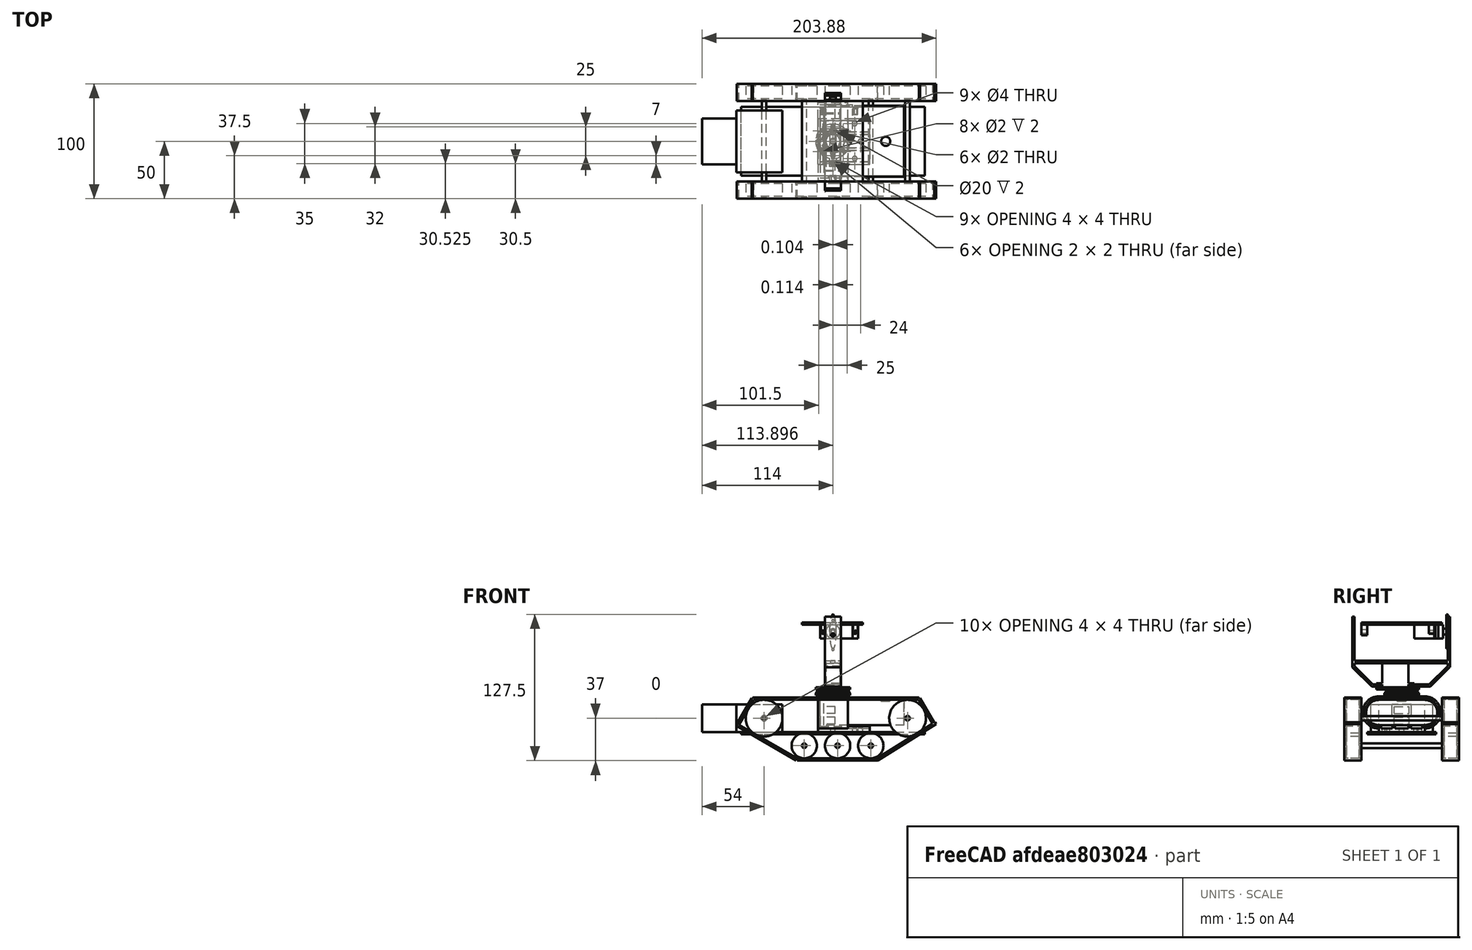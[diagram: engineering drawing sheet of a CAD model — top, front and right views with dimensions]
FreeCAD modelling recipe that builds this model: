
FCSTD DOCUMENT
Label: androidtank_8
License: CC-BY 3.0
LicenseURL: http://creativecommons.org/licenses/by/3.0/
objects: Part::Cylinder×56, Part::Box×36, Part::MultiFuse×25, Part::Sphere×8, Part::Cut×7, Part::FeaturePython×1, App::DocumentObjectGroup×1
note: 133 computed .brp shape members not serialized (recipe doc carries the construction recipe); baked Part::Feature solids carry a one-line shape summary decoded from their .brp

FEATURE [Part::Box] Box  label="MainFrame"
  Height = 2
  Length = 160
  Width = 60
FEATURE [Part::Box] Box001001  label="Moter Unit2"
  Height = 24
  Length = 30
  Placement = pos=(-34,10,2) rot=(0,0,1;0rad)
  Width = 40
FEATURE [Part::Cylinder] Cylinder  label="Shaft"
  Angle = 360
  Height = 100
  Placement = pos=(20,-20,14) rot=(-1,0,0;1.5708rad)
  Radius = 2
FEATURE [Part::Box] Box001002
  Height = 2
  Length = 145
  Placement = pos=(10,-20,30) rot=(0,0,1;0rad)
  Width = 15
FEATURE [Part::Box] Box001002001
  Height = 2
  Length = 70
  Placement = pos=(49,-20,-23) rot=(0,0,1;0rad)
  Width = 15
FEATURE [Part::Box] Box001002001001
  Height = 2
  Length = 60
  Placement = pos=(119,-20,-23) rot=(0,-1,0;0.558505rad)
  Width = 15
FEATURE [Part::Box] Box001002001002
  Height = 2
  Length = 60
  Placement = pos=(49,-20,-21) rot=(0,1,0;3.66519rad)
  Width = 15
FEATURE [Part::Box] Box001002001003
  Height = 2
  Length = 26
  Placement = pos=(-2,-20,8) rot=(0,-1,0;1.0472rad)
  Width = 15
FEATURE [Part::Box] Box001002001003001
  Height = 2
  Length = 26
  Placement = pos=(169,-20,9) rot=(0,-1,0;2.0944rad)
  Width = 15
FEATURE [Part::MultiFuse] Fusion002001002  label="Caterpiller1"
  Shapes = -> [Box001002,Box001002001,Box001002001002,Box001002001001,Box001002001003,Box001002001003001]
FEATURE [Part::MultiFuse] Fusion002001002001  label="Caterpiller2"
  Placement = pos=(0,85,0) rot=(0,0,1;0rad)
  Shapes = -> [Box001002,Box001002001,Box001002001002,Box001002001001,Box001002001003,Box001002001003001]
FEATURE [Part::Cylinder] Cylinder002001001002  label="Wheel006"
  Angle = 360
  Height = 11
  Placement = pos=(20,78,14) rot=(1,0,0;1.5708rad)
  Radius = 11
FEATURE [Part::Cylinder] Cylinder002001001002001  label="Wheel007"
  Angle = 360
  Height = 11
  Placement = pos=(20,-7,14) rot=(1,0,0;1.5708rad)
  Radius = 11
FEATURE [Part::Cylinder] Cylinder002001002001  label="Shaft002"
  Angle = 360
  Height = 100
  Placement = pos=(20,-20,14) rot=(-1,0,0;1.5708rad)
  Radius = 2
FEATURE [Part::MultiFuse] Fusion002001002002002  label="SWheelSet1"
  Placement = pos=(35,0,-24) rot=(0,0,1;0rad)
  Shapes = -> [Cylinder002001002001,Cylinder002001001002,Cylinder002001001002001]
FEATURE [Part::MultiFuse] Fusion002001002002002001  label="SWheelSet2"
  Placement = pos=(64,0,-24) rot=(0,0,1;0rad)
  Shapes = -> [Cylinder002001002001,Cylinder002001001002,Cylinder002001001002001]
FEATURE [Part::MultiFuse] Fusion002001002002002001001  label="SWheelSet3"
  Placement = pos=(93,0,-24) rot=(0,0,1;0rad)
  Shapes = -> [Cylinder002001002001,Cylinder002001001002,Cylinder002001001002001]
FEATURE [Part::Box] Box001002001003002
  Height = 22
  Length = 70
  Placement = pos=(0,0,-11) rot=(0,0,1;0rad)
  Width = 40
FEATURE [Part::Cylinder] Cylinder002001001002002
  Angle = 360
  Height = 70
  Placement = pos=(0,0,0) rot=(0,1,0;1.5708rad)
  Radius = 11
FEATURE [Part::Cylinder] Cylinder001
  Angle = 360
  Height = 70
  Placement = pos=(0,40,0) rot=(0,1,0;1.5708rad)
  Radius = 11
FEATURE [Part::Cylinder] Cylinder002001001002003  label="PowerButton"
  Angle = 360
  Height = 2
  Placement = pos=(16,20,10) rot=(0,0,1;0rad)
  Radius = 4
FEATURE [Part::Box] Box001002001003003  label="USB1"
  Height = 6
  Length = 15
  Placement = pos=(60,13.5,-1) rot=(0,0,1;0rad)
  Width = 13
FEATURE [Part::Box] Box001001001  label="USB2"
  Height = 6
  Length = 15
  Placement = pos=(60,13.5,-10) rot=(0,0,1;0rad)
  Width = 13
FEATURE [Part::MultiFuse] Fusion002001002002002001002
  Shapes = -> [Cylinder001,Box001002001003002,Cylinder002001001002002]
FEATURE [Part::MultiFuse] Fusion001001
  Shapes = -> [Box001001001,Cylinder002001001002003,Box001002001003003]
FEATURE [Part::Cut] Cut  label="Eneloop"
  Base = -> Fusion002001002002002001002
  Placement = pos=(142,50,19) rot=(0,0,1;3.14159rad)
  Tool = -> Fusion001001
FEATURE [Part::Cylinder] Cylinder001001  label="Cylinder002"
  Angle = 360
  Height = 26
  Placement = pos=(0,50,19) rot=(0,1,0;1.5708rad)
  Radius = 14
FEATURE [Part::Box] Box001002001003002001  label="Box001002001003002001001001001006001001002001003001006"
  Height = 28
  Length = 26
  Placement = pos=(0,10,5) rot=(0,0,1;0rad)
  Width = 40
FEATURE [Part::Cylinder] Cylinder002001001002002001  label="Cylinder003"
  Angle = 360
  Height = 26
  Placement = pos=(0,10,19) rot=(0,1,0;1.5708rad)
  Radius = 14
FEATURE [Part::Box] Box001  label="Moter Unit1"
  Height = 24
  Length = 40
  Placement = pos=(-4,3,2) rot=(0,0,1;0rad)
  Width = 54
FEATURE [Part::Box] Box001002001003002001001  label="Box003"
  Height = 5
  Length = 45
  Placement = pos=(0,10,2) rot=(0,0,1;0rad)
  Width = 40
FEATURE [Part::Box] Box001002001003002001002  label="Box004"
  Height = 24
  Length = 26
  Placement = pos=(2,10,7) rot=(0,0,1;0rad)
  Width = 40
FEATURE [Part::Cylinder] Cylinder001001001  label="Cylinder004"
  Angle = 360
  Height = 26
  Placement = pos=(2,50,19) rot=(0,1,0;1.5708rad)
  Radius = 12
FEATURE [Part::Cylinder] Cylinder002001001002002001001  label="Cylinder005"
  Angle = 360
  Height = 26
  Placement = pos=(2,10,19) rot=(0,1,0;1.5708rad)
  Radius = 12
FEATURE [Part::Box] Box001002001003002001001001  label="Box006"
  Height = 3
  Length = 45
  Placement = pos=(2,12,5) rot=(0,0,1;0rad)
  Width = 10
FEATURE [Part::Box] Box001002001003002001001001001  label="Box007"
  Height = 3
  Length = 45
  Placement = pos=(2,24,5) rot=(0,0,1;0rad)
  Width = 12
FEATURE [Part::Box] Box001002001003002001001001001001  label="Box008"
  Height = 3
  Length = 45
  Placement = pos=(2,38,5) rot=(0,0,1;0rad)
  Width = 10
FEATURE [Part::MultiFuse] Fusion002001002002002001003
  Shapes = -> [Box001002001003002001,Cylinder001001,Cylinder002001001002002001,Box001002001003002001001]
FEATURE [Part::Cylinder] Cylinder002001001002002001002001  label="Cylinder007"
  Angle = 360
  Height = 40
  Placement = pos=(80,17.5,0) rot=(0,0,1;0rad)
  Radius = 1
FEATURE [Part::Cylinder] Cylinder002001001002002001002  label="Cylinder006"
  Angle = 360
  Height = 40
  Placement = pos=(80,42.5,0) rot=(0,0,1;0rad)
  Radius = 1
FEATURE [Part::Cylinder] Cylinder002001001002002001002001001  label="Cylinder008"
  Angle = 360
  Height = 40
  Placement = pos=(104,30,0) rot=(0,0,1;0rad)
  Radius = 2
FEATURE [Part::Cylinder] Cylinder002001001002002001002001002  label="Cylinder009"
  Angle = 360
  Height = 40
  Placement = pos=(99,45.5,0) rot=(0,0,1;0rad)
  Radius = 2
FEATURE [Part::Cylinder] Cylinder002001001002002001002001003  label="Cylinder0010"
  Angle = 360
  Height = 40
  Placement = pos=(99,15,0) rot=(0,0,1;0rad)
  Radius = 2
FEATURE [Part::Box] Box001002001003002001001001001006  label="Box009"
  Height = 2
  Length = 53
  Placement = pos=(47,-5,100) rot=(0,0,1;0rad)
  Width = 70
FEATURE [Part::Box] Box001002001003002001001001001006001  label="Box010"
  Height = 44
  Length = 14
  Placement = pos=(67,70,66) rot=(0,0,1;0rad)
  Width = 2
FEATURE [Part::Box] Box001002001003002001001001001006001001  label="Box011"
  Height = 2
  Length = 13
  Placement = pos=(67.5,12.5,48) rot=(0,0,1;0rad)
  Width = 23.5
FEATURE [Part::Box] Box001002001003002001001001001006001001001  label="Box012"
  Height = 44
  Length = 14
  Placement = pos=(67,-13,66) rot=(0,0,1;0rad)
  Width = 2
FEATURE [Part::Cylinder] Cylinder002001001002002001002001008  label="Hole1"
  Angle = 360
  Height = 20
  Placement = pos=(74,-20,94) rot=(-1,0,0;1.5708rad)
  Radius = 1.5
FEATURE [Part::Cylinder] Cylinder002001001002002001002001008001  label="Hole2"
  Angle = 360
  Height = 20
  Placement = pos=(74,60,106.5) rot=(-1,0,0;1.5708rad)
  Radius = 1
FEATURE [Part::Cylinder] Cylinder002001001002002001002001008001001  label="Hole4"
  Angle = 360
  Height = 20
  Placement = pos=(74,38.5,41) rot=(0,0,1;0rad)
  Radius = 1
FEATURE [Part::Cylinder] Cylinder002001001002002001002001008001001001  label="Hole3"
  Angle = 360
  Height = 20
  Placement = pos=(74,60,81.5) rot=(-1,0,0;1.5708rad)
  Radius = 1
FEATURE [Part::Cylinder] Cylinder002001001002002001002001008001001002  label="Hole5"
  Angle = 360
  Height = 20
  Placement = pos=(74,10.5,41) rot=(0,0,1;0rad)
  Radius = 1
FEATURE [Part::Box] Box001002001003002001001001001006001001001001  label="Box013"
  Height = 24
  Length = 14
  Placement = pos=(67,4,49) rot=(1,0,0;0.785397rad)
  Width = 2
FEATURE [Part::Box] Box001002001003002001001001001006001001001001001  label="Box014"
  Height = 24
  Length = 14
  Placement = pos=(67,53.41,50.41) rot=(-1,0,0;0.785397rad)
  Width = 2
FEATURE [Part::Box] Box001002001003002001001001001006001001002001  label="Box016"
  Height = 2
  Length = 14
  Placement = pos=(67,4,49) rot=(0,0,1;0rad)
  Width = 9
FEATURE [Part::Box] Box001002001003002001001001001006001001002001001  label="Box017"
  Height = 2
  Length = 14
  Placement = pos=(67,36,49) rot=(0,0,1;0rad)
  Width = 19
FEATURE [Part::Box] Box001002001003002001001001001006001001002001002  label="Box015"
  Height = 2
  Length = 14
  Placement = pos=(67,-13,69.5) rot=(0,0,1;0rad)
  Width = 85
FEATURE [Part::MultiFuse] Fusion002001002002002001009
  Shapes = -> [Box001002001003002001001001001006001,Box001002001003002001001001001006001001001001,Box001002001003002001001001001006001001001,Box001002001003002001001001001006001001001001001,Box001002001003002001001001001006001001002001,Box001002001003002001001001001006001001002001002,Box001002001003002001001001001006001001002001001]
FEATURE [Part::Cylinder] Cylinder002001001002002001002001008001001002001  label="Hole006"
  Angle = 360
  Height = 20
  Placement = pos=(74,10.5,60) rot=(0,0,1;0rad)
  Radius = 2
FEATURE [Part::Cylinder] Cylinder002001001002002001002001008001001002002  label="Hole007"
  Angle = 360
  Height = 20
  Placement = pos=(74,38.5,60) rot=(0,0,1;0rad)
  Radius = 2
FEATURE [Part::MultiFuse] Fusion002001002002002001010
  Shapes = -> [Cylinder002001001002002001002001008001,Box001002001003002001001001001006001001,Cylinder002001001002002001002001008001001,Cylinder002001001002002001002001008,Cylinder002001001002002001002001008001001001,Cylinder002001001002002001002001008001001002,Cylinder002001001002002001002001008001001002002,Cylinder002001001002002001002001008001001002001]
FEATURE [Part::Cut] Cut003  label="HeadFrame"
  Base = -> Fusion002001002002002001009
  Placement = pos=(6,0,-7.5) rot=(0,0,1;0rad)
  Tool = -> Fusion002001002002002001010
FEATURE [Part::Cylinder] Cylinder002001001002002001002001008001001002003  label="Cylinder025"
  Angle = 360
  Height = 5
  Placement = pos=(74,0,94) rot=(1,0,0;1.5708rad)
  Radius = 3
FEATURE [Part::Box] Box001002001003002001001001001006001001002001003  label="Box020"
  Height = 6
  Length = 6
  Placement = pos=(71,-5,94) rot=(0,0,1;0rad)
  Width = 5
FEATURE [Part::Cylinder] Cylinder002001001002002001002001008001001002003001  label="Cylinder026"
  Angle = 360
  Height = 7
  Placement = pos=(74,1,94) rot=(1,0,0;1.5708rad)
  Radius = 1.5
FEATURE [Part::Box] Box001002001003002001001001001006001001002001003001001  label="Box022"
  Height = 6
  Length = 4
  Placement = pos=(91.5,53.5,94) rot=(0,0,1;0rad)
  Width = 5
FEATURE [Part::Cylinder] Cylinder002001001002002001002001008001001002003002  label="Cylinder027"
  Angle = 360
  Height = 5
  Placement = pos=(65.5,58.5,94) rot=(1,0,0;1.5708rad)
  Radius = 2
FEATURE [Part::Cylinder] Cylinder002001001002002001002001008001001002003002001  label="Cylinder028"
  Angle = 360
  Height = 5
  Placement = pos=(93.5,58.5,94) rot=(1,0,0;1.5708rad)
  Radius = 2
FEATURE [Part::Box] Box001002001003002001001001001006001001002001003001  label="Box021"
  Height = 6
  Length = 4
  Placement = pos=(63.5,53.5,94) rot=(0,0,1;0rad)
  Width = 5
FEATURE [Part::Cylinder] Cylinder002001001002002001002001008001001002003002002  label="Cylinder029"
  Angle = 360
  Height = 6
  Placement = pos=(65.5,59,94) rot=(1,0,0;1.5708rad)
  Radius = 1
FEATURE [Part::Cylinder] Cylinder002001001002002001002001008001001002003002001001  label="Cylinder030"
  Angle = 360
  Height = 6
  Placement = pos=(93.5,59,94) rot=(1,0,0;1.5708rad)
  Radius = 1
FEATURE [Part::MultiFuse] Fusion002001002002002001011
  Shapes = -> [Box001002001003002001001001001006,Box001002001003002001001001001006001001002001003001001,Cylinder002001001002002001002001008001001002003002001,Box001002001003002001001001001006001001002001003,Cylinder002001001002002001002001008001001002003,Box001002001003002001001001001006001001002001003001,Cylinder002001001002002001002001008001001002003002]
FEATURE [Part::MultiFuse] Fusion002001002002002001012
  Shapes = -> [Cylinder002001001002002001002001008001001002003001,Cylinder002001001002002001002001008001001002003002002,Cylinder002001001002002001002001008001001002003002001001]
FEATURE [Part::Cut] Cut002003  label="HeadMount"
  Base = -> Fusion002001002002002001011
  Placement = pos=(6,0,-4.5) rot=(0,0,1;0rad)
  Tool = -> Fusion002001002002002001012
FEATURE [Part::Cylinder] Cylinder002001001002002001002001001001  label="Cylinder040"
  Angle = 360
  Height = 40
  Placement = pos=(80,30,0) rot=(0,0,1;0rad)
  Radius = 2
FEATURE [Part::Box] Box001002001003002001001001001006001001002001003001002  label="ServoBody"
  Height = 21
  Length = 23
  Width = 12
FEATURE [Part::Cylinder] Cylinder002001001002002001002001008001001002003002001002  label="ServoBody2"
  Angle = 360
  Height = 4
  Placement = pos=(6,6,21) rot=(0,0,1;0rad)
  Radius = 6
FEATURE [Part::Box] Box001002001003002001001001001006001001002001003001003  label="ServoBody3"
  Height = 1
  Length = 33
  Placement = pos=(-5,0,17.5) rot=(0,0,1;0rad)
  Width = 12
FEATURE [Part::Cylinder] Cylinder001001002  label="ServoAxis"
  Angle = 360
  Height = 4
  Placement = pos=(6,6,24) rot=(0,0,1;0rad)
  Radius = 2.5
FEATURE [Part::MultiFuse] Fusion005  label="ServoArmL"
  Shapes = -> [Cylinder001001002,Box001002001003002001001001001006001001002001003001003,Box001002001003002001001001001006001001002001003001002,Cylinder002001001002002001002001008001001002003002001002]
FEATURE [Part::MultiFuse] Fusion006  label="ServoYaw"
  Placement = pos=(86,36,62) rot=(0.707107,-0.707107,0;3.14159rad)
  Shapes = -> [Fusion005]
FEATURE [Part::Cylinder] Cylinder003001001004  label="Cylinder002001001002002001002001008001001002003002001006"
  Angle = 360
  Height = 0.5
  Placement = pos=(-2.5,6,20.5) rot=(0,0,1;0rad)
  Radius = 2
FEATURE [Part::Cylinder] Cylinder003001001005  label="Cylinder011"
  Angle = 360
  Height = 2
  Placement = pos=(6,6,21) rot=(0,0,1;0rad)
  Radius = 15
FEATURE [Part::Cylinder] Cylinder003001001004001  label="Cylinder010"
  Angle = 360
  Height = 0.5
  Placement = pos=(25.5,6,20.5) rot=(0,0,1;0rad)
  Radius = 2
FEATURE [Part::Cylinder] Cylinder003001001005001  label="Cylinder012"
  Angle = 360
  Height = 2
  Placement = pos=(6,6,21) rot=(0,0,1;0rad)
  Radius = 6.5
FEATURE [Part::Cylinder] Cylinder003001001005001001  label="Cylinder013"
  Angle = 360
  Height = 2
  Placement = pos=(12,6,21) rot=(0,0,1;0rad)
  Radius = 3.5
FEATURE [Part::Box] Box002
  Height = 2
  Length = 10
  Placement = pos=(18,3,21) rot=(0,0,1;0rad)
  Width = 6
FEATURE [Part::Cylinder] Cylinder003001001004002  label="Cylinder014"
  Angle = 360
  Height = 5
  Placement = pos=(-2.5,6,19.5) rot=(0,0,1;0rad)
  Radius = 1
FEATURE [Part::Cylinder] Cylinder003001001004001001  label="Cylinder015"
  Angle = 360
  Height = 5
  Placement = pos=(25.5,6,19.5) rot=(0,0,1;0rad)
  Radius = 1
FEATURE [Part::MultiFuse] Fusion008
  Shapes = -> [Cylinder003001001005,Box002,Cylinder003001001004,Cylinder003001001004001]
FEATURE [Part::MultiFuse] Fusion009
  Shapes = -> [Cylinder003001001005001,Cylinder003001001005001001,Cylinder003001001004002,Cylinder003001001004001001]
FEATURE [Part::Cut] Cut002  label="Guide1"
  Base = -> Fusion008
  Placement = pos=(86,36,62) rot=(-0.705662,0.708549,0;3.14159rad)
  Tool = -> Fusion009
FEATURE [Part::Box] Box001002001003002001001001001006001001002001003001004  label="ServoBody004"
  Height = 21
  Length = 23
  Width = 12
FEATURE [Part::Cylinder] Cylinder002001001002002001002001008001001002003002001003  label="ServoBody005"
  Angle = 360
  Height = 4
  Placement = pos=(6,6,21) rot=(0,0,1;0rad)
  Radius = 6
FEATURE [Part::Box] Box001002001003002001001001001006001001002001003001005  label="ServoBody006"
  Height = 1
  Length = 33
  Placement = pos=(-5,0,17.5) rot=(0,0,1;0rad)
  Width = 12
FEATURE [Part::Cylinder] Cylinder001001003  label="ServoAxis001"
  Angle = 360
  Height = 4
  Placement = pos=(6,6,24) rot=(0,0,1;0rad)
  Radius = 2.5
FEATURE [Part::MultiFuse] Fusion005001  label="ServoArmL001"
  Shapes = -> [Cylinder001001003,Box001002001003002001001001001006001001002001003001005,Box001002001003002001001001001006001001002001003001004,Cylinder002001001002002001002001008001001002003002001003]
FEATURE [Part::Cylinder] Cylinder002001001002002001002001008001001002003002001004  label="Cylinder002001001002002001002001008001001002003002001012"
  Angle = 360
  Height = 2
  Radius = 2.5
FEATURE [Part::FeaturePython] Scale  # Draft clone (typed FeaturePython)
  Objects = -> [Cylinder002001001002002001002001008001001002003002001004]
  Placement = pos=(0,0,1) rot=(0,0,1;0rad)
  Scale = (6,1,0.5)
FEATURE [Part::MultiFuse] Fusion  label="Arm"
  Placement = pos=(6,6,27) rot=(0,0,1;1.5708rad)
  Shapes = -> [Cylinder002001001002002001002001008001001002003002001004,Scale]
FEATURE [Part::MultiFuse] Fusion006001  label="ServoPitch"
  Placement = pos=(74,41,95.5) rot=(-1,0,0;1.5708rad)
  Shapes = -> [Fusion005001,Fusion]
FEATURE [Part::Cylinder] Cylinder002001001002002001002001008001001002003002001005  label="Wheel1"
  Angle = 360
  Height = 11
  Placement = pos=(20,78,14) rot=(1,0,0;1.5708rad)
  Radius = 16
FEATURE [Part::Cylinder] Cylinder002001001002002001002001008001001002003002001005001  label="Wheel2"
  Angle = 360
  Height = 11
  Placement = pos=(20,-7,14) rot=(1,0,0;1.5708rad)
  Radius = 16
FEATURE [Part::MultiFuse] Fusion002001002002002001014  label="LWheelSet1"
  Shapes = -> [Cylinder,Cylinder002001001002002001002001008001001002003002001005,Cylinder002001001002002001002001008001001002003002001005001]
FEATURE [Part::MultiFuse] Fusion002001002002002001014001  label="LWheelSet2"
  Placement = pos=(125,0,0) rot=(0,0,1;0rad)
  Shapes = -> [Cylinder,Cylinder002001001002002001002001008001001002003002001005,Cylinder002001001002002001002001008001001002003002001005001]
FEATURE [App::DocumentObjectGroup] ____________  label="DriveFrame"
  Group = -> [Box,Box001,Box001001,Fusion002001002,Fusion002001002001,Fusion002001002002002,Fusion002001002002002001,Fusion002001002002002001001,Fusion002001002002002001014,Fusion002001002002002001014001]
FEATURE [Part::Cylinder] Cylinder003001001003  label="Cylinder002001001002002001002001008001001002003002001013"
  Angle = 360
  Height = 2
  Placement = pos=(6,6,26) rot=(0,0,1;0rad)
  Radius = 15
FEATURE [Part::Sphere] Sphere
  Angle1 = -90
  Angle2 = 0
  Angle3 = 360
  Placement = pos=(-3,-3,26) rot=(0,0,1;0rad)
  Radius = 2
FEATURE [Part::Sphere] Sphere001
  Angle1 = -90
  Angle2 = 0
  Angle3 = 360
  Placement = pos=(15,-3,26) rot=(0,0,1;0rad)
  Radius = 2
FEATURE [Part::Sphere] Sphere001001  label="Sphere002"
  Angle1 = -90
  Angle2 = 0
  Angle3 = 360
  Placement = pos=(15,15,26) rot=(0,0,1;0rad)
  Radius = 2
FEATURE [Part::Sphere] Sphere001001001  label="Sphere003"
  Angle1 = -90
  Angle2 = 0
  Angle3 = 360
  Placement = pos=(-3,15,26) rot=(0,0,1;0rad)
  Radius = 2
FEATURE [Part::Cylinder] Cylinder003001001005001004  label="Cylinder020"
  Angle = 360
  Height = 4
  Placement = pos=(-6.5,6,26) rot=(0,0,1;0rad)
  Radius = 1
FEATURE [Part::Cylinder] Cylinder003001001001003  label="Cylinder021"
  Angle = 360
  Height = 4
  Placement = pos=(18.5,6,26) rot=(0,0,1;0rad)
  Radius = 1
FEATURE [Part::Cylinder] Cylinder003001001005001003001  label="Cylinder022"
  Angle = 360
  Height = 5
  Placement = pos=(-3,-3,26) rot=(0,0,1;0rad)
  Radius = 1
FEATURE [Part::Cylinder] Cylinder003001001001002001  label="Cylinder023"
  Angle = 360
  Height = 5
  Placement = pos=(15,-3,26) rot=(0,0,1;0rad)
  Radius = 1
FEATURE [Part::Sphere] Sphere001001001001  label="Sphere004"
  Angle1 = -90
  Angle2 = 0
  Angle3 = 360
  Placement = pos=(-6.5,6,26) rot=(0,0,1;0rad)
  Radius = 2
FEATURE [Part::Sphere] Sphere001001001001001  label="Sphere005"
  Angle1 = -90
  Angle2 = 0
  Angle3 = 360
  Placement = pos=(18.5,6,26) rot=(0,0,1;0rad)
  Radius = 2
FEATURE [Part::Sphere] Sphere001001001001001001  label="Sphere006"
  Angle1 = -90
  Angle2 = 0
  Angle3 = 360
  Placement = pos=(6,-6.5,26) rot=(0,0,1;0rad)
  Radius = 2
FEATURE [Part::Sphere] Sphere001001001001001001001  label="Sphere007"
  Angle1 = -90
  Angle2 = 0
  Angle3 = 360
  Placement = pos=(6,18.5,26) rot=(0,0,1;0rad)
  Radius = 2
FEATURE [Part::Cylinder] Cylinder003001001003001  label="Cylinder024"
  Angle = 360
  Height = 2
  Placement = pos=(6,6,26) rot=(0,0,1;0rad)
  Radius = 10
FEATURE [Part::MultiFuse] Fusion014
  Shapes = -> [Sphere,Cylinder003001001003,Sphere001001001,Sphere001001001001001001,Sphere001001001001,Sphere001,Sphere001001,Sphere001001001001001001001,Sphere001001001001001]
FEATURE [Part::Cylinder] Cylinder003001001005001003001001  label="Cylinder002001001002002001002001008001001002003002001014"
  Angle = 360
  Height = 5
  Placement = pos=(-3,15,26) rot=(0,0,1;0rad)
  Radius = 1
FEATURE [Part::Cylinder] Cylinder003001001001002001001  label="Cylinder002001001002002001002001008001001002003002001015"
  Angle = 360
  Height = 5
  Placement = pos=(15,15,26) rot=(0,0,1;0rad)
  Radius = 1
FEATURE [Part::Cylinder] Cylinder003001001005001003001001001  label="Cylinder002001001002002001002001008001001002003002001016"
  Angle = 360
  Height = 5
  Placement = pos=(6,18.5,26) rot=(0,0,1;0rad)
  Radius = 1
FEATURE [Part::Cylinder] Cylinder003001001005001003001001001001  label="Cylinder002001001002002001002001008001001002003002001017"
  Angle = 360
  Height = 5
  Placement = pos=(6,-6.5,26) rot=(0,0,1;0rad)
  Radius = 1
FEATURE [Part::MultiFuse] Fusion015
  Shapes = -> [Cylinder003001001003001,Cylinder003001001005001004,Cylinder003001001001003,Cylinder003001001005001003001,Cylinder003001001001002001,Cylinder003001001005001003001001,Cylinder003001001005001003001001001001,Cylinder003001001001002001001,Cylinder003001001005001003001001001]
FEATURE [Part::Cut] Cut002005  label="Guide2"
  Base = -> Fusion014
  Placement = pos=(74,36,62) rot=(1,0,0;3.14159rad)
  Tool = -> Fusion015
FEATURE [Part::MultiFuse] Fusion002001002002002001014002
  Shapes = -> [Box001002001003002001002,Cylinder001001001,Cylinder002001001002002001001,Box001002001003002001001001,Box001002001003002001001001001,Box001002001003002001001001001001]
FEATURE [Part::Cut] Cut002006
  Base = -> Fusion002001002002002001003
  Placement = pos=(67,0,0) rot=(0,0,1;0rad)
  Tool = -> Fusion002001002002002001014002
FEATURE [Part::Cylinder] Cylinder002001001002002001002001001001001  label="Cylinder041"
  Angle = 360
  Height = 20
  Placement = pos=(80,42.5,0) rot=(0,0,1;0rad)
  Radius = 2
FEATURE [Part::Cylinder] Cylinder002001001002002001002001001001001001  label="Cylinder042"
  Angle = 360
  Height = 20
  Placement = pos=(80,17.5,0) rot=(0,0,1;0rad)
  Radius = 2
FEATURE [Part::Box] Box001002001003003001  label="USB003"
  Height = 10
  Length = 15
  Placement = pos=(60,21.5,16) rot=(0,0,1;0rad)
  Width = 17
FEATURE [Part::MultiFuse] Fusion002001002002002001014003
  Shapes = -> [Cylinder002001001002002001002001,Cylinder002001001002002001002,Cylinder002001001002002001002001001,Cylinder002001001002002001002001002,Cylinder002001001002002001002001003,Cylinder002001001002002001002001001001,Cylinder002001001002002001002001001001001,Box001002001003003001,Cylinder002001001002002001002001001001001001]
FEATURE [Part::Cut] Cut002007  label="BatteryFrame2"
  Base = -> Cut002006
  Tool = -> Fusion002001002002002001014003
